# Revit family: Zumtobel LINETIK D-I
name_source: partatom
category: Lighting Fixtures
revit_build: Autodesk Revit 2016 (Build: 20150220_1215(x64)
units: mm (PartAtom-declared; Revit-internal decimal feet)

## family parameters
Cut with Voids When Loaded = No
Host = Face
Light Source = Yes
OmniClass Number = 23.80.70.11
OmniClass Title = Luminaries for Internal Lighting
Part Type = Normal
Room Calculation Point = No
Round Connector Dimension = Use Diameter
Shared = No

## types (3) — shared parameters
Assembly Code = D5020200
Color Filter = 16777215
Cover = Zumtobel_Cover_Self_llumination_Opaque
Description = Pendant LED luminaire
Dimming Lamp Color Temperature Shift = <None>
Emit Shape Visible in Rendering = No
Emit from Rectangle Length = 25 mm  [stored 0.082021 ft]
Emit from Rectangle Width = 1000 mm  [stored 3.28084 ft]
Height = 25 mm  [stored 0.082021 ft]
Lamp = LED
Length = 1474 mm  [stored 4.83596 ft]
Manufacturer = Zumtobel Lighting
Suspension = Zumtobel_Metal_White
Tilt Angle = -90.00°
URL = http://www.zumtobel.com
Width = 25 mm  [stored 0.082021 ft]
zero-valued in all types: Default Elevation

## per-type parameters (varying)
| type | Apparent Load | Body | Model | Photometric Web File |
| LINETIK D/I – Black | 50 VA | Zumtobel_Metal_Black | 42930320 | D40767oAA_D40769uAA_LINETIK-P_DI_LED6000-830_BK.IES |
| LINETIK D/I – Silver | 50 VA | Zumtobel_Metal_Silver | 42930319 | D40767oAA_D40769uAA_LINETIK-P_DI_LED6000-830_SR.IES |
| LINETIK D/I – White | 47 VA | Zumtobel_Metal_White | 42930318 | D40767oAA_D40769uAA_LINETIK-P_DI_LED6000-830_WH.IES |

note: [stored X ft] marks values corroborated as IEEE doubles in the binary element streams (Revit-internal decimal feet)

## geometry (parser evidence)
native form markers: Sweep x2
no freeform markers — native parametric forms only
